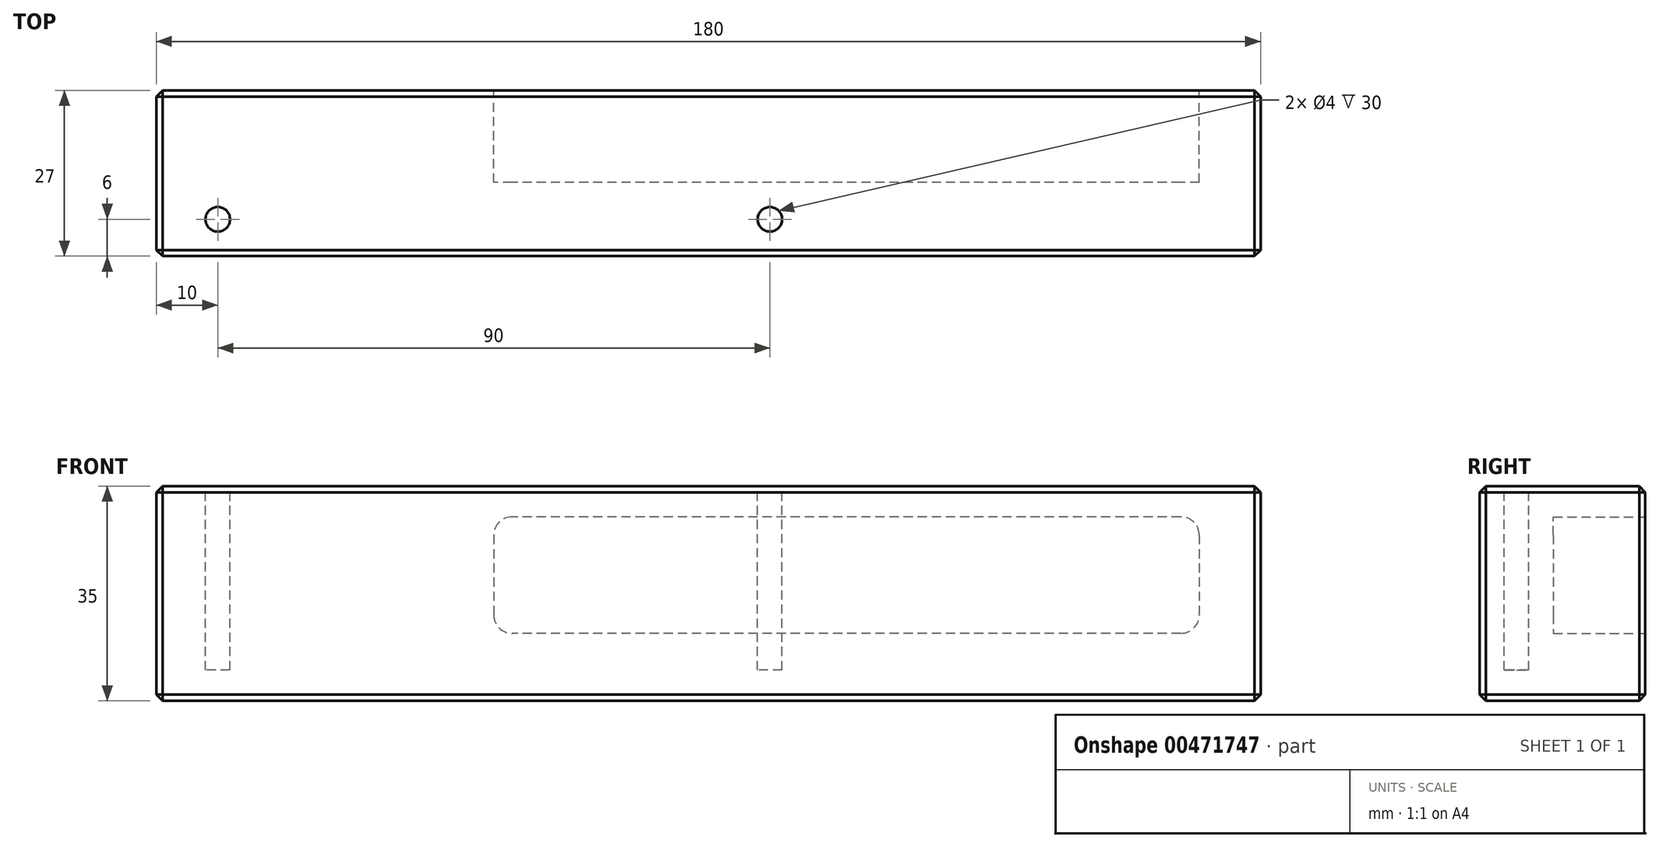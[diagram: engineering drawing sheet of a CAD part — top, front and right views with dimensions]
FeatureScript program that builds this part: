
annotation { "Feature Type Name" : "Feature", "Feature Type Description" : "" }
export const myFeature = defineFeature(function(context is Context, id is Id, definition is map)
    precondition{}
    {
        {
            var Q0;
            Q0=qCreatedBy(makeId("Front.planeOp"),FACE);
            var sketch = newSketch(context, id + "F0", { "sketchPlane" : qUnion([Q0])});
            skLineSegment(sketch, "E0.bottom", {"start": v(90, -17.5) * mm, "end": v(-90, -17.5) * mm});
            skLineSegment(sketch, "E0.top", {"start": v(90, 17.5) * mm, "end": v(-90, 17.5) * mm});
            skLineSegment(sketch, "E0.left", {"start": v(90, -17.5) * mm, "end": v(90, 17.5) * mm});
            skLineSegment(sketch, "E0.right", {"start": v(-90, -17.5) * mm, "end": v(-90, 17.5) * mm});
            skPoint(sketch, "E0.middle", {"position": v(0, 0) * mm});
            skSolve(sketch);
        }
        {
            var Q0;
            Q0=makeQuery(id+"F0.imprint","IMPRINT",FACE,{"disambiguationData":[TD([[makeQuery(id+"F0.imprint","IMPRINT",EDGE,{"derivedFrom":sQuery(id+"F0.wireOp",EDGE,"E0.bottom")}),-1.0]])]});
            extrude(context, id + "F1", {"entities" : qUnion([Q0]), "depth" : 27 * mm});
        }
        {
            var Q0;
            Q0=makeQuery(id+"F1.opExtrude","CAP_FACE",FACE,{"disambiguationData":[OSD([sQuery(id+"F0.wireOp",EDGE,"E0.bottom"),sQuery(id+"F0.wireOp",EDGE,"E0.top"),sQuery(id+"F0.wireOp",EDGE,"E0.left"),sQuery(id+"F0.wireOp",EDGE,"E0.right")])],"isStart":true});
            var sketch = newSketch(context, id + "F2", { "sketchPlane" : qUnion([Q0])});
            skLineSegment(sketch, "E1.bottom", {"start": v(-77, 12.5) * mm, "end": v(32, 12.5) * mm});
            skLineSegment(sketch, "E1.top", {"start": v(-77, -6.5) * mm, "end": v(32, -6.5) * mm});
            skLineSegment(sketch, "E1.left", {"start": v(-80, 9.5) * mm, "end": v(-80, -3.5) * mm});
            skLineSegment(sketch, "E1.right", {"start": v(35, 9.5) * mm, "end": v(35, -3.5) * mm});
            skPoint(sketch, "E2.visualSharp", {"position": v(-80, 12.5) * mm});
            skArc(sketch, "E2.filletArc", {"start": v(-77, 12.5) * mm, "mid": v(-79.12, 11.62) * mm, "end": v(-80, 9.5) * mm});
            skPoint(sketch, "E3.visualSharp", {"position": v(-80, -6.5) * mm});
            skArc(sketch, "E3.filletArc", {"start": v(-80, -3.5) * mm, "mid": v(-79.12, -5.62) * mm, "end": v(-77, -6.5) * mm});
            skPoint(sketch, "E4.visualSharp", {"position": v(35, -6.5) * mm});
            skArc(sketch, "E4.filletArc", {"start": v(32, -6.5) * mm, "mid": v(34.12, -5.62) * mm, "end": v(35, -3.5) * mm});
            skPoint(sketch, "E5.visualSharp", {"position": v(35, 12.5) * mm});
            skArc(sketch, "E5.filletArc", {"start": v(35, 9.5) * mm, "mid": v(34.12, 11.62) * mm, "end": v(32, 12.5) * mm});
            skSolve(sketch);
        }
        {
            var Q0;
            Q0=makeQuery(id+"F2.imprint","IMPRINT",FACE,{"disambiguationData":[TD([[makeQuery(id+"F2.imprint","IMPRINT",EDGE,{"derivedFrom":sQuery(id+"F2.wireOp",EDGE,"E1.bottom")}),-1.0]])]});
            extrude(context, id + "F3", {"entities" : qUnion([Q0]), "operationType" : NewBodyOperationType.REMOVE, "oppositeDirection" : true, "depth" : 15 * mm});
        }
        {
            var Q0;
            Q0=makeQuery(id+"F1.opExtrude","SWEPT_EDGE",EDGE,{"disambiguationData":[OSD([sQuery(id+"F0.wireOp",EDGE,"E0.bottom"),sQuery(id+"F0.wireOp",EDGE,"E0.right")])]});
            var Q1;
            Q1=makeQuery(id+"F1.opExtrude","SWEPT_EDGE",EDGE,{"disambiguationData":[OSD([sQuery(id+"F0.wireOp",EDGE,"E0.top"),sQuery(id+"F0.wireOp",EDGE,"E0.right")])]});
            var Q2;
            Q2=makeQuery(id+"F1.opExtrude","SWEPT_EDGE",EDGE,{"disambiguationData":[OSD([sQuery(id+"F0.wireOp",EDGE,"E0.bottom"),sQuery(id+"F0.wireOp",EDGE,"E0.left")])]});
            var Q3;
            Q3=makeQuery(id+"F1.opExtrude","SWEPT_EDGE",EDGE,{"disambiguationData":[OSD([sQuery(id+"F0.wireOp",EDGE,"E0.top"),sQuery(id+"F0.wireOp",EDGE,"E0.left")])]});
            var Q4;
            Q4=makeQuery(id+"F1.opExtrude","CAP_EDGE",EDGE,{"disambiguationData":[OSD([sQuery(id+"F0.wireOp",EDGE,"E0.top")])],"isStart":true});
            var Q5;
            Q5=makeQuery(id+"F1.opExtrude","CAP_EDGE",EDGE,{"disambiguationData":[OSD([sQuery(id+"F0.wireOp",EDGE,"E0.bottom")])],"isStart":true});
            var Q6;
            Q6=makeQuery(id+"F1.opExtrude","CAP_EDGE",EDGE,{"disambiguationData":[OSD([sQuery(id+"F0.wireOp",EDGE,"E0.left")])],"isStart":false});
            var Q7;
            Q7=makeQuery(id+"F1.opExtrude","CAP_EDGE",EDGE,{"disambiguationData":[OSD([sQuery(id+"F0.wireOp",EDGE,"E0.left")])],"isStart":true});
            var Q8;
            Q8=makeQuery(id+"F1.opExtrude","CAP_EDGE",EDGE,{"disambiguationData":[OSD([sQuery(id+"F0.wireOp",EDGE,"E0.right")])],"isStart":true});
            var Q9;
            Q9=makeQuery(id+"F1.opExtrude","CAP_EDGE",EDGE,{"disambiguationData":[OSD([sQuery(id+"F0.wireOp",EDGE,"E0.right")])],"isStart":false});
            var Q10;
            Q10=makeQuery(id+"F1.opExtrude","CAP_FACE",FACE,{"disambiguationData":[OSD([sQuery(id+"F0.wireOp",EDGE,"E0.bottom"),sQuery(id+"F0.wireOp",EDGE,"E0.top"),sQuery(id+"F0.wireOp",EDGE,"E0.left"),sQuery(id+"F0.wireOp",EDGE,"E0.right")])],"isStart":false});
            chamfer(context, id + "F4", {"entities" : qUnion([Q0, Q1, Q2, Q3, Q4, Q5, Q6, Q7, Q8, Q9, Q10]), "width" : 1 * mm, "tangentPropagation" : true});
        }
        {
            var Q0;
            Q0=makeQuery(id+"F1.opExtrude","SWEPT_FACE",FACE,{"disambiguationData":[OSD([sQuery(id+"F0.wireOp",EDGE,"E0.top")])]});
            var sketch = newSketch(context, id + "F5", { "sketchPlane" : qUnion([Q0])});
            skCircle(sketch, "E6", {"center": v(-80, -21) * mm, "radius": 2 * mm});
            skCircle(sketch, "E7", {"center": v(10, -21) * mm, "radius": 2 * mm});
            skSolve(sketch);
        }
        {
            var Q0;
            Q0=makeQuery(id+"F5.imprint","IMPRINT",FACE,{"disambiguationData":[TD([[makeQuery(id+"F5.imprint","IMPRINT",EDGE,{"derivedFrom":sQuery(id+"F5.wireOp",EDGE,"E6")}),1.0]])]});
            var Q1;
            Q1=makeQuery(id+"F5.imprint","IMPRINT",FACE,{"disambiguationData":[TD([[makeQuery(id+"F5.imprint","IMPRINT",EDGE,{"derivedFrom":sQuery(id+"F5.wireOp",EDGE,"E7")}),1.0]])]});
            extrude(context, id + "F6", {"entities" : qUnion([Q0, Q1]), "operationType" : NewBodyOperationType.REMOVE, "oppositeDirection" : true, "depth" : 30 * mm});
        }
    });
